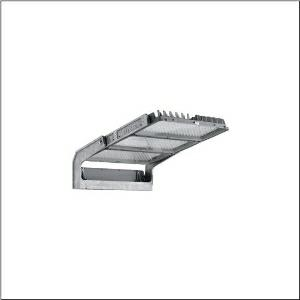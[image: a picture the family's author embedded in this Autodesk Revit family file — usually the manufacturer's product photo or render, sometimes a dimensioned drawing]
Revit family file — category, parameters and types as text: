
# Revit family: floodlight_fl_11_maxi_pro___rs07_5xa779124k01ab_afb2
name_source: partatom
category: Lighting Fixtures
units: mm (PartAtom-declared; Revit-internal decimal feet)

## family parameters
Cut with Voids When Loaded = No
Host = Face
Light Source = No
Part Type = Normal
Room Calculation Point = No
Round Connector Dimension = Use Diameter
Shared = No

## types (1)
- --- (1 x LED, 153810 lm, 1633.1 W, 5700K)
    Apparent Load = 1633 VA
    CIE Flux Codes = 80 93 99 100 99
    Color Rendering = 90
    Color Temperature = 5700K
    Default Elevation = 1800 mm
    Description = Floodlight FL 11  maxi  pro floodlight; light control with lens of PMMA; cover panel of toughened safety glass, transparent; light distribution: RS07, rotationally symmetric direct distribution, LEDcolour temperature: 5700K, rated luminous flux: 153.810lm, colour rendering: CRI > 90, light colour: 957; luminous efficacy: 94lm/W; brightness control: DALI 2; with terminal, 5-pole, max. 2.5mm², mains connection: 220..240V/380..400V AC, 50/60Hz, surge voltage resistance: line to ground: 10kV, service life up to 100,000h L90. Typical operating time: 1000h per year, ECG replaceable separately, LED unit replaceable without ESD environment, dustproof LED module, dimming range 10..100%; 1633W floodlight with 3x LED unit of diecast aluminium, coated grey; length: 1.003mm / width: 651mm / height: 338mm; mounting bracket, of diecast aluminium, uncoated, natural, protection rating (complete): IP66; insulation class (complete): insulation class I (protective earthing); certification: CE, ENEC, VDE; ball protection: ball impact resistant, only for outdoor installations in the designated locations, permissible operating ambient temperature: -40..+55°C, permissible storage temperature: -40..+85°Cpackaging unit: 1 piece

Light Distribution: RS07
    Height = 320 mm
    Lamp = 1 x LED
    Lamp Light Flux = 153810 lm
    Lamp Power = 1633.1 W
    Lamp count = 1
    Length = 1002 mm
    Luminous efficacy = 94 lm/W
    Manufacturer = Siteco
    ModVariant = No
    Model = 5XA779124K01AB
    Mounting Place = Ceiling
    Mounting Type = Surface mounted
    Number of Poles = 1
    OnlyDefault = Yes
    Power Factor = 1
    Product Name = Floodlight FL 11 maxi pro | RS07
    Product group = floodlight | ceiling mounted
    ProductGroupID = 301
    Protection Class = Protection class I
    Protection Degree = IP 66
    RLX_Detail_Level = 1
    RLX_Emergency_Light_Flux = 0 lm
    RLX_Emergency_Type = 0
    RLX_Emergency_Type_DB = No
    RlxData = <blob elided: 40109 chars, md5=938964bc>
    Socket = socket
    Standby Power = 0 W
    System Light Flux = 153810 lm
    System Power = 1633 W
    Type Comments = factory setting: luminous flux: 100 % | dim-lin: 254 | 1100 mA
    Type Image = l_1356210.jpg
    URL = http://relux.com
    VarID = @adj_023836
    Voltage = 0 V
    Weight = 0.00 kg
    Width = 655 mm

## geometry (parser evidence)
native form markers: Blend x4, Sweep x15
no freeform markers — native parametric forms only
